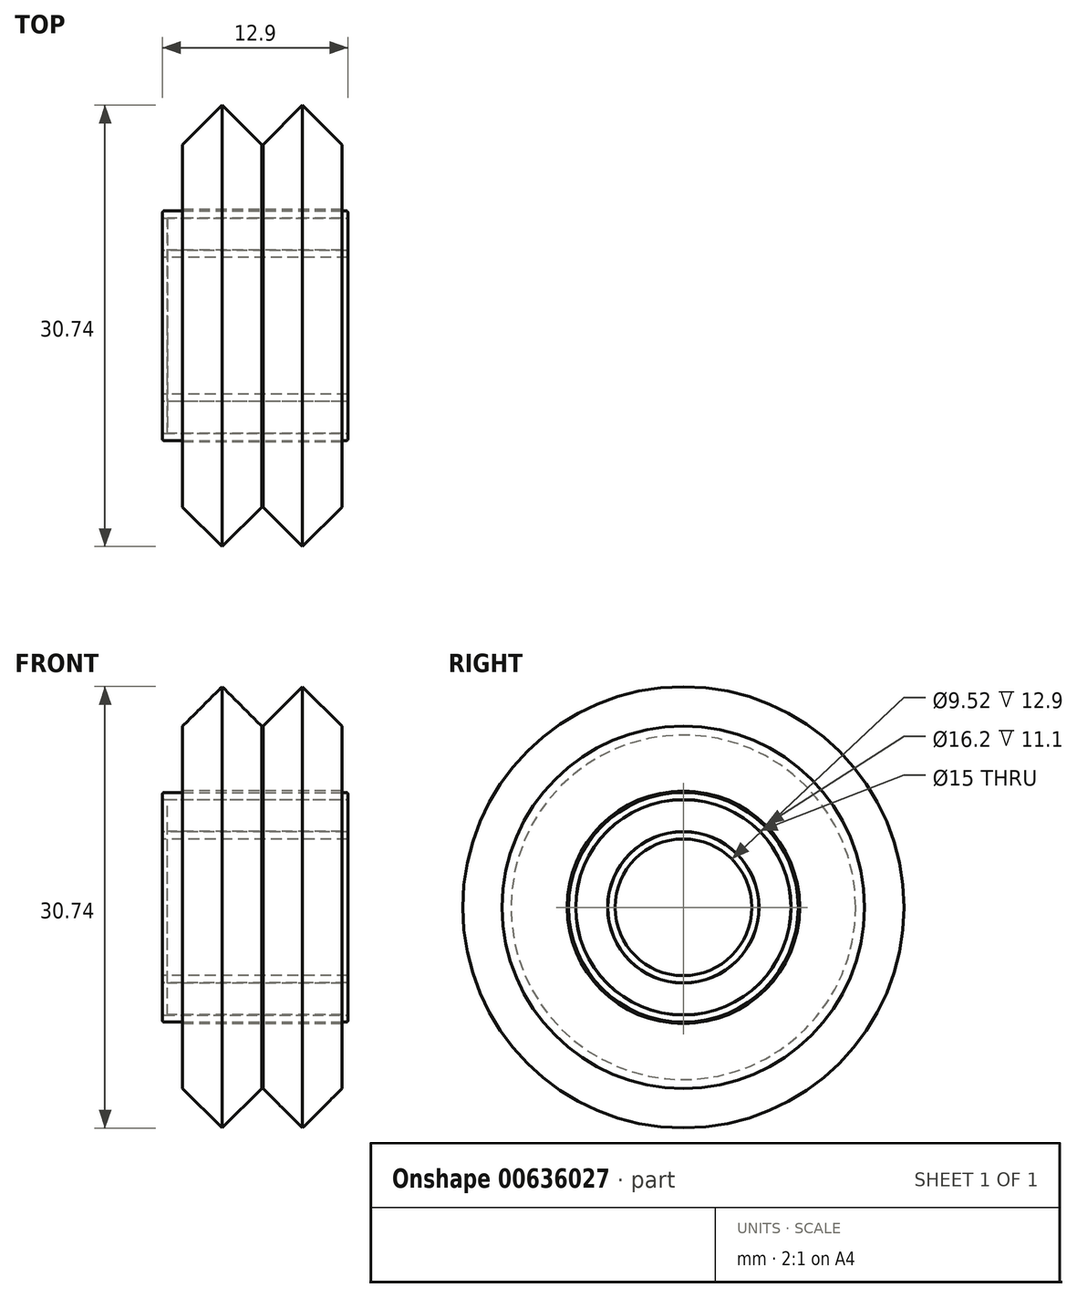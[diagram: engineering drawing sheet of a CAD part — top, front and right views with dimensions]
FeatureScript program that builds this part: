
annotation { "Feature Type Name" : "Feature", "Feature Type Description" : "" }
export const myFeature = defineFeature(function(context is Context, id is Id, definition is map)
    precondition{}
    {
        {
            var Q0;
            Q0=qCreatedBy(makeId("Right.planeOp"),FACE);
            var sketch = newSketch(context, id + "F0", { "sketchPlane" : qUnion([Q0])});
            skCircle(sketch, "E0", {"center": v(0, 0) * mm, "radius": 15.37 * mm});
            skCircle(sketch, "E1", {"center": v(0, 0) * mm, "radius": 4.76 * mm});
            skSolve(sketch);
        }
        {
            var Q0;
            Q0=makeQuery(id+"F0.imprint","IMPRINT",FACE,{"disambiguationData":[TD([[makeQuery(id+"F0.imprint","IMPRINT",EDGE,{"derivedFrom":sQuery(id+"F0.wireOp",EDGE,"E0")}),1.0]])]});
            extrude(context, id + "F1", {"entities" : qUnion([Q0]), "depth" : 5.5 * mm, "offsetDistance" : 25 * mm});
        }
        {
            var Q0;
            Q0=qCreatedBy(makeId("Right.planeOp"),FACE);
            var sketch = newSketch(context, id + "F2", { "sketchPlane" : qUnion([Q0])});
            skCircle(sketch, "E2", {"center": v(0, 0) * mm, "radius": 12 * mm});
            skSolve(sketch);
        }
        {
            var Q0;
            Q0 = qSketchRegion(id + "F2", true);
            extrude(context, id + "F3", {"entities" : qUnion([Q0]), "operationType" : NewBodyOperationType.ADD, "oppositeDirection" : true, "depth" : .1 * mm, "offsetDistance" : 25 * mm});
        }
        {
            var Q0;
            Q0=makeQuery(id+"F3.opExtrude","CAP_FACE",FACE,{"disambiguationData":[OSD([sQuery(id+"F2.wireOp",EDGE,"E2")])],"isStart":false});
            var sketch = newSketch(context, id + "F4", { "sketchPlane" : qUnion([Q0])});
            skCircle(sketch, "E3", {"center": v(0, 0) * mm, "radius": 15.36 * mm});
            skSolve(sketch);
        }
        {
            var Q0;
            Q0=makeQuery(id+"F4.imprint","IMPRINT",FACE,{"disambiguationData":[TD([[makeQuery(id+"F4.imprint","IMPRINT",EDGE,{"derivedFrom":sQuery(id+"F4.wireOp",EDGE,"E3")}),1.0]])]});
            var Q1;
            Q1=makeQuery(id+"F4.imprint","IMPRINT",FACE,{"disambiguationData":[TD([[makeQuery(id+"F4.imprint","IMPRINT",EDGE,{"derivedFrom":makeQuery(id+"F3.opExtrude","CAP_EDGE",EDGE,{"disambiguationData":[OSD([sQuery(id+"F2.wireOp",EDGE,"E2")])],"isStart":false})}),-1.0]])]});
            extrude(context, id + "F5", {"entities" : qUnion([Q0, Q1]), "operationType" : NewBodyOperationType.ADD, "depth" : 5.5 * mm, "offsetDistance" : 25 * mm});
        }
        {
            var Q0;
            Q0=makeQuery(id+"F1.opExtrude","CAP_EDGE",EDGE,{"disambiguationData":[OSD([sQuery(id+"F0.wireOp",EDGE,"E0")])],"isStart":false});
            var Q1;
            Q1=makeQuery(id+"F1.opExtrude","CAP_EDGE",EDGE,{"disambiguationData":[OSD([sQuery(id+"F0.wireOp",EDGE,"E0")])],"isStart":true});
            var Q2;
            Q2=makeQuery(id+"F5.opExtrude","CAP_EDGE",EDGE,{"disambiguationData":[OSD([sQuery(id+"F4.wireOp",EDGE,"E3")])],"isStart":true});
            var Q3;
            Q3=makeQuery(id+"F5.opExtrude","CAP_EDGE",EDGE,{"disambiguationData":[OSD([sQuery(id+"F4.wireOp",EDGE,"E3")])],"isStart":false});
            chamfer(context, id + "F6", {"entities" : qUnion([Q0, Q1, Q2, Q3]), "chamferType" : ChamferType.OFFSET_ANGLE, "width" : 2.75 * mm, "oppositeDirection" : false, "angle" : 45 * degree, "tangentPropagation" : true});
        }
        {
            var Q0;
            Q0=qCreatedBy(makeId("Right.planeOp"),FACE);
            var sketch = newSketch(context, id + "F7", { "sketchPlane" : qUnion([Q0])});
            skCircle(sketch, "E4", {"center": v(0, 0) * mm, "radius": 8.1 * mm});
            skSolve(sketch);
        }
        {
            var Q0;
            Q0 = qSketchRegion(id + "F7", true);
            extrude(context, id + "F8", {"entities" : qUnion([Q0]), "operationType" : NewBodyOperationType.REMOVE, "depth" : 25 * mm, "offsetDistance" : 25 * mm, "symmetric" : true});
        }
        {
            var Q0;
            Q0=makeQuery(id+"F1.opExtrude","CAP_FACE",FACE,{"disambiguationData":[OSD([sQuery(id+"F0.wireOp",EDGE,"E0"),sQuery(id+"F0.wireOp",EDGE,"E1")])],"isStart":false});
            var sketch = newSketch(context, id + "F9", { "sketchPlane" : qUnion([Q0])});
            skCircle(sketch, "E5", {"center": v(0, 0) * mm, "radius": 4.76 * mm});
            skCircle(sketch, "E6", {"center": v(0, 0) * mm, "radius": 5.26 * mm});
            skCircle(sketch, "E7", {"center": v(0, 0) * mm, "radius": 7.5 * mm});
            skCircle(sketch, "E8", {"center": v(0, 0) * mm, "radius": 8 * mm});
            skSolve(sketch);
        }
        {
            var Q0;
            Q0=makeQuery(id+"F9.imprint","IMPRINT",FACE,{"disambiguationData":[TD([[makeQuery(id+"F9.imprint","IMPRINT",EDGE,{"derivedFrom":sQuery(id+"F9.wireOp",EDGE,"E7")}),-1.0]])]});
            extrude(context, id + "F10", {"entities" : qUnion([Q0]), "operationType" : NewBodyOperationType.ADD, "oppositeDirection" : true, "depth" : 12.5 * mm, "offsetDistance" : 25 * mm});
        }
        {
            var Q0;
            Q0=makeQuery(id+"F9.imprint","IMPRINT",FACE,{"disambiguationData":[TD([[makeQuery(id+"F9.imprint","IMPRINT",EDGE,{"derivedFrom":sQuery(id+"F9.wireOp",EDGE,"E7")}),-1.0]])]});
            extrude(context, id + "F11", {"entities" : qUnion([Q0]), "operationType" : NewBodyOperationType.ADD, "depth" : .4 * mm, "offsetDistance" : 25 * mm});
        }
        {
            var Q0;
            Q0=makeQuery(id+"F9.imprint","IMPRINT",FACE,{"disambiguationData":[TD([[makeQuery(id+"F9.imprint","IMPRINT",EDGE,{"derivedFrom":sQuery(id+"F9.wireOp",EDGE,"E6")}),1.0]])]});
            extrude(context, id + "F12", {"entities" : qUnion([Q0]), "operationType" : NewBodyOperationType.ADD, "depth" : .4 * mm, "offsetDistance" : 25 * mm});
        }
        {
            var Q0;
            Q0=makeQuery(id+"F12.opExtrude","CAP_FACE",FACE,{"disambiguationData":[OSD([sQuery(id+"F0.wireOp",EDGE,"E1"),sQuery(id+"F9.wireOp",EDGE,"E6")])],"isStart":false});
            extrude(context, id + "F13", {"entities" : qUnion([Q0]), "operationType" : NewBodyOperationType.ADD, "oppositeDirection" : true, "depth" : 12.9 * mm, "offsetDistance" : 25 * mm});
        }
        {
            var Q0;
            Q0=makeQuery(id+"F10.opExtrude","CAP_EDGE",EDGE,{"disambiguationData":[OSD([sQuery(id+"F9.wireOp",EDGE,"E7")])],"isStart":false});
            var Q1;
            Q1=makeQuery(id+"F13.opExtrude","CAP_EDGE",EDGE,{"disambiguationData":[OSD([sQuery(id+"F9.wireOp",EDGE,"E6")])],"isStart":false});
            var Q2;
            Q2=makeQuery(id+"F10.opExtrude","CAP_EDGE",EDGE,{"disambiguationData":[OSD([sQuery(id+"F9.wireOp",EDGE,"E8")])],"isStart":false});
            var Q3;
            Q3=makeQuery(id+"F13.opExtrude","CAP_EDGE",EDGE,{"disambiguationData":[OSD([sQuery(id+"F0.wireOp",EDGE,"E1")])],"isStart":false});
            var Q4;
            Q4=makeQuery(id+"F12.opExtrude","CAP_EDGE",EDGE,{"disambiguationData":[OSD([sQuery(id+"F9.wireOp",EDGE,"E6")])],"isStart":false});
            var Q5;
            Q5=makeQuery(id+"F12.opExtrude","CAP_EDGE",EDGE,{"disambiguationData":[OSD([sQuery(id+"F0.wireOp",EDGE,"E1")])],"isStart":false});
            var Q6;
            Q6=makeQuery(id+"F11.opExtrude","CAP_EDGE",EDGE,{"disambiguationData":[OSD([sQuery(id+"F9.wireOp",EDGE,"E7")])],"isStart":false});
            var Q7;
            Q7=makeQuery(id+"F11.opExtrude","CAP_EDGE",EDGE,{"disambiguationData":[OSD([sQuery(id+"F9.wireOp",EDGE,"E8")])],"isStart":false});
            fillet(context, id + "F14", {"entities" : qUnion([Q0, Q1, Q2, Q3, Q4, Q5, Q6, Q7]), "radius" : .1 * mm, "tangentPropagation" : true, "allowEdgeOverflow" : false});
        }
        {
            var Q0;
            Q0=qCreatedBy(makeId("Right.planeOp"),FACE);
            var sketch = newSketch(context, id + "F15", { "sketchPlane" : qUnion([Q0])});
            skCircle(sketch, "E9", {"center": v(0, 0) * mm, "radius": 5.28 * mm});
            skCircle(sketch, "E10", {"center": v(0, 0) * mm, "radius": 7.5 * mm});
            skSolve(sketch);
        }
        {
            var Q0;
            Q0=makeQuery(id+"F15.imprint","IMPRINT",FACE,{"disambiguationData":[TD([[makeQuery(id+"F15.imprint","IMPRINT",EDGE,{"derivedFrom":sQuery(id+"F15.wireOp",EDGE,"E9")}),-1.0]])]});
            extrude(context, id + "F16", {"entities" : qUnion([Q0]), "depth" : 5.5 * mm, "offsetDistance" : 25 * mm});
        }
        {
            var Q0;
            Q0=makeQuery(id+"F16.opExtrude","CAP_FACE",FACE,{"disambiguationData":[OSD([sQuery(id+"F15.wireOp",EDGE,"E9"),sQuery(id+"F15.wireOp",EDGE,"E10")])],"isStart":true});
            extrude(context, id + "F17", {"entities" : qUnion([Q0]), "operationType" : NewBodyOperationType.ADD, "depth" : 6.65 * mm, "offsetDistance" : 25 * mm});
        }
    });
